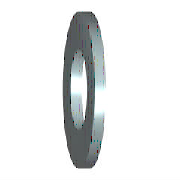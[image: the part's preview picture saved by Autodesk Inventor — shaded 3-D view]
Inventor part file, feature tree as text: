
AUTODESK INVENTOR PART (.ipt)
format: ipt  version: 2020 (Build 240168000, 168)  size: 109,056 bytes
history: native  units: mm (DEFAULTED — no unit token found)
features: other x1, plane x1, sketch x1
ambient origin geometry x7: Origin, YZ Plane, XY Plane, X Axis, Y Axis, Z Axis, Center Point
bodies: Solid1 (feature_tree), Body (feature_tree)
feature tree (3):
  other  "Work Axis1"
  plane  "Work Plane1"
  sketch  "Sketch"  dims[d0=4.3mm d1=9.0mm d2=0.8mm d3=0.0mm d4=0.0mm d5=0.0mm d6=0.0mm d7=0.0mm]
